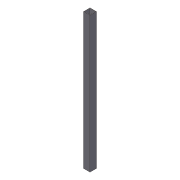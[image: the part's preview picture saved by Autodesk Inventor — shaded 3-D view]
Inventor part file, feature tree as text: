
AUTODESK INVENTOR PART (.ipt)
format: ipt  version: 2012 (Build 160160000, 160)  size: 70,656 bytes
history: native  units: in
note: dims shown in document units (in); Inventor stores cm internally (conversion verified against a paired STEP export)
features: extrude x1, shell x1, sketch x1
ambient origin geometry x8: Origin, YZ Plane, XZ Plane, XY Plane, X Axis, Y Axis, Z Axis, Center Point
bodies: Solid1 (feature_tree)
feature tree (3):
  extrude  "Extrusion1"  Depth=1.0in
  shell  "Shell1"  Thickness=1.0in
  sketch  "Sketch1"  dims[d0=21.0in d1=1.0in d2=1.0in d3=0.0in d4=0.0625in]
